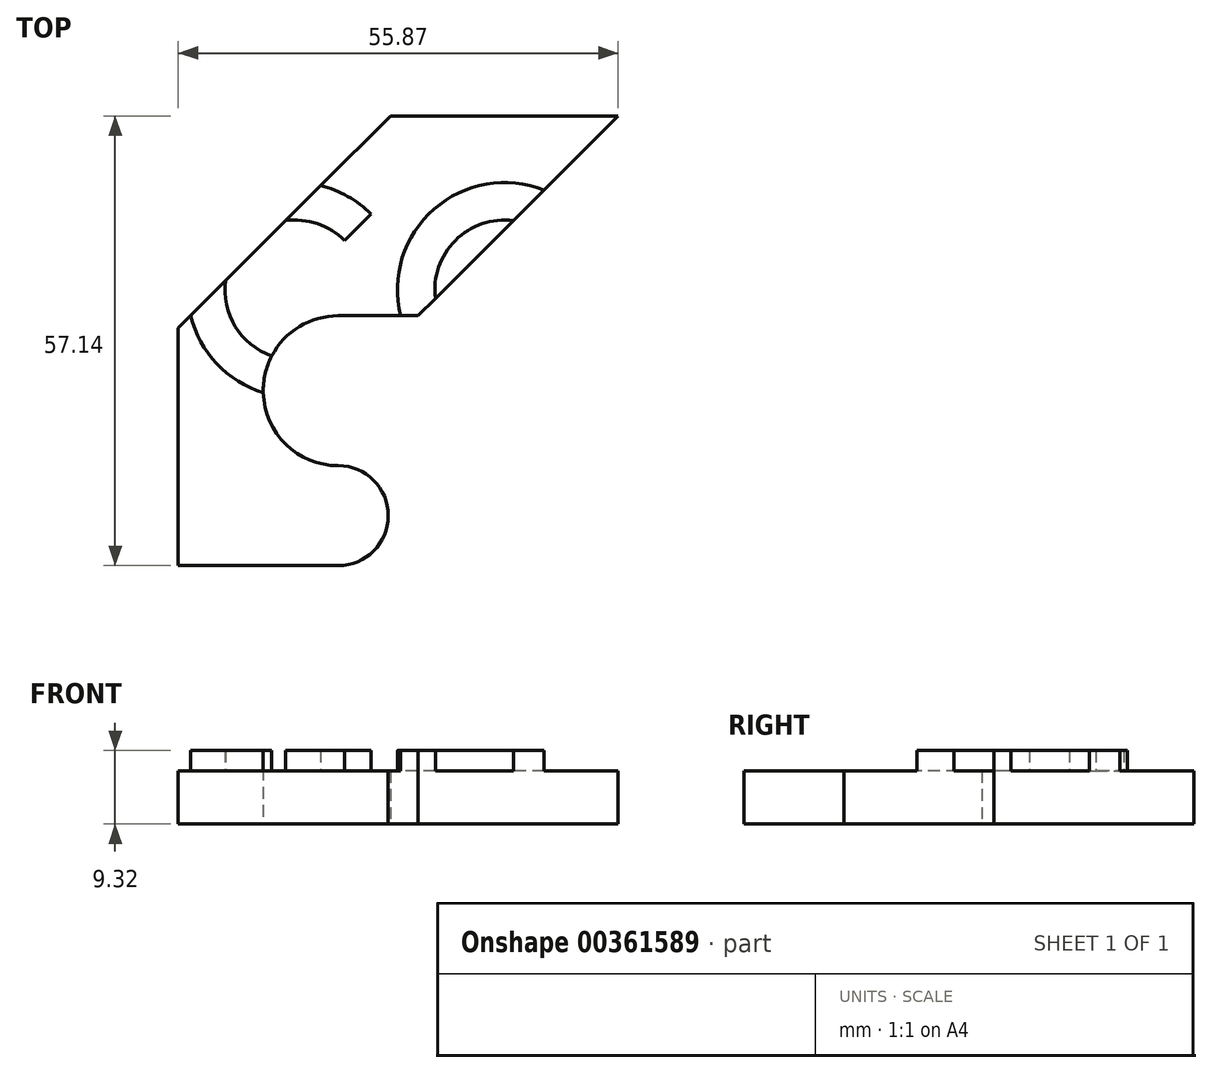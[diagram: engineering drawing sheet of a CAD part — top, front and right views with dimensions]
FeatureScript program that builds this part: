
annotation { "Feature Type Name" : "Feature", "Feature Type Description" : "" }
export const myFeature = defineFeature(function(context is Context, id is Id, definition is map)
    precondition{}
    {
        {
            var Q0;
            Q0=qCreatedBy(makeId("Top.planeOp"),FACE);
            var sketch = newSketch(context, id + "F0", { "sketchPlane" : qUnion([Q0])});
            skArc(sketch, "E0", {"start": v(0, -6.35) * mm, "mid": v(6.35, 0) * mm, "end": v(0, 6.35) * mm});
            skLineSegment(sketch, "E1", {"start": v(0, 25.4) * mm, "end": v(10.16, 25.4) * mm});
            skLineSegment(sketch, "E2", {"start": v(10.16, 25.4) * mm, "end": v(35.55, 50.8) * mm});
            skLineSegment(sketch, "E3", {"start": v(35.55, 50.8) * mm, "end": v(6.62, 50.8) * mm});
            skLineSegment(sketch, "E4", {"start": v(6.62, 50.8) * mm, "end": v(-20.32, 23.85) * mm});
            skLineSegment(sketch, "E5", {"start": v(-20.32, 23.85) * mm, "end": v(-20.32, -6.35) * mm});
            skLineSegment(sketch, "E6", {"start": v(-20.32, -6.35) * mm, "end": v(0, -6.35) * mm});
            skArc(sketch, "E7", {"start": v(0, 25.4) * mm, "mid": v(-9.53, 15.88) * mm, "end": v(0, 6.35) * mm});
            skPoint(sketch, "E7.second.point", {"position": v(0, 6.35) * mm});
            skPoint(sketch, "E7.third.point", {"position": v(9.49, 16.7) * mm});
            skSolve(sketch);
        }
        {
            var Q0;
            Q0 = qSketchRegion(id + "F0", true);
            extrude(context, id + "F1", {"entities" : qUnion([Q0]), "depth" : 6.73 * mm});
        }
        {
            var Q0;
            Q0=makeQuery(id+"F1.opExtrude","CAP_FACE",FACE,{"disambiguationData":[OSD([sQuery(id+"F0.wireOp",EDGE,"E0"),sQuery(id+"F0.wireOp",EDGE,"E1"),sQuery(id+"F0.wireOp",EDGE,"E2"),sQuery(id+"F0.wireOp",EDGE,"E3"),sQuery(id+"F0.wireOp",EDGE,"E4"),sQuery(id+"F0.wireOp",EDGE,"E5"),sQuery(id+"F0.wireOp",EDGE,"E6"),sQuery(id+"F0.wireOp",EDGE,"E7")])],"isStart":false});
            var sketch = newSketch(context, id + "F2", { "sketchPlane" : qUnion([Q0])});
            skLineSegment(sketch, "E8", {"start": v(-20.32, 13.83) * mm, "end": v(16.64, 50.8) * mm, "construction": true});
            skLineSegment(sketch, "E9", {"start": v(6.62, 50.8) * mm, "end": v(16.64, 50.8) * mm, "construction": true});
            skArc(sketch, "E10", {"start": v(-14.3, 29.88) * mm, "mid": v(-13.08, 24.04) * mm, "end": v(-8.45, 20.28) * mm});
            skArc(sketch, "E11", {"start": v(-18.75, 25.42) * mm, "mid": v(-15.43, 19.3) * mm, "end": v(-9.52, 15.62) * mm});
            skLineSegment(sketch, "E12", {"start": v(-20.32, 23.85) * mm, "end": v(6.62, 50.8) * mm, "construction": true});
            skArc(sketch, "E13", {"start": v(-8.45, 20.28) * mm, "mid": v(-9.28, 18.02) * mm, "end": v(-9.52, 15.62) * mm});
            skArc(sketch, "E14.trimOffspring", {"start": v(4.17, 38.32) * mm, "mid": v(1.2, 40.56) * mm, "end": v(-2.25, 41.92) * mm});
            skArc(sketch, "E15.trimOffspring", {"start": v(0.8, 34.95) * mm, "mid": v(-2.66, 37.09) * mm, "end": v(-6.7, 37.47) * mm});
            skArc(sketch, "E16", {"start": v(22.26, 37.5) * mm, "mid": v(14.87, 34.96) * mm, "end": v(12.34, 27.58) * mm});
            skArc(sketch, "E17", {"start": v(26.15, 41.39) * mm, "mid": v(12.16, 38.94) * mm, "end": v(7.9, 25.4) * mm});
            skLineSegment(sketch, "E18", {"start": v(0, 25.4) * mm, "end": v(10.16, 25.4) * mm, "construction": true});
            skLineSegment(sketch, "E19", {"start": v(10.16, 25.4) * mm, "end": v(27.92, 43.16) * mm, "construction": true});
            skLineSegment(sketch, "E20", {"start": v(0.8, 34.95) * mm, "end": v(4.17, 38.32) * mm});
            skLineSegment(sketch, "E21", {"start": v(-6.7, 37.47) * mm, "end": v(-2.25, 41.92) * mm});
            skLineSegment(sketch, "E22", {"start": v(-14.3, 29.88) * mm, "end": v(-18.75, 25.42) * mm});
            skLineSegment(sketch, "E23", {"start": v(7.9, 25.4) * mm, "end": v(10.16, 25.4) * mm});
            skLineSegment(sketch, "E24", {"start": v(22.26, 37.5) * mm, "end": v(26.15, 41.39) * mm});
            skLineSegment(sketch, "E25", {"start": v(10.16, 25.4) * mm, "end": v(12.34, 27.58) * mm});
            skSolve(sketch);
        }
        {
            var Q0;
            Q0 = qSketchRegion(id + "F2", true);
            extrude(context, id + "F3", {"entities" : qUnion([Q0]), "operationType" : NewBodyOperationType.ADD, "depth" : 2.6 * mm});
        }
    });
